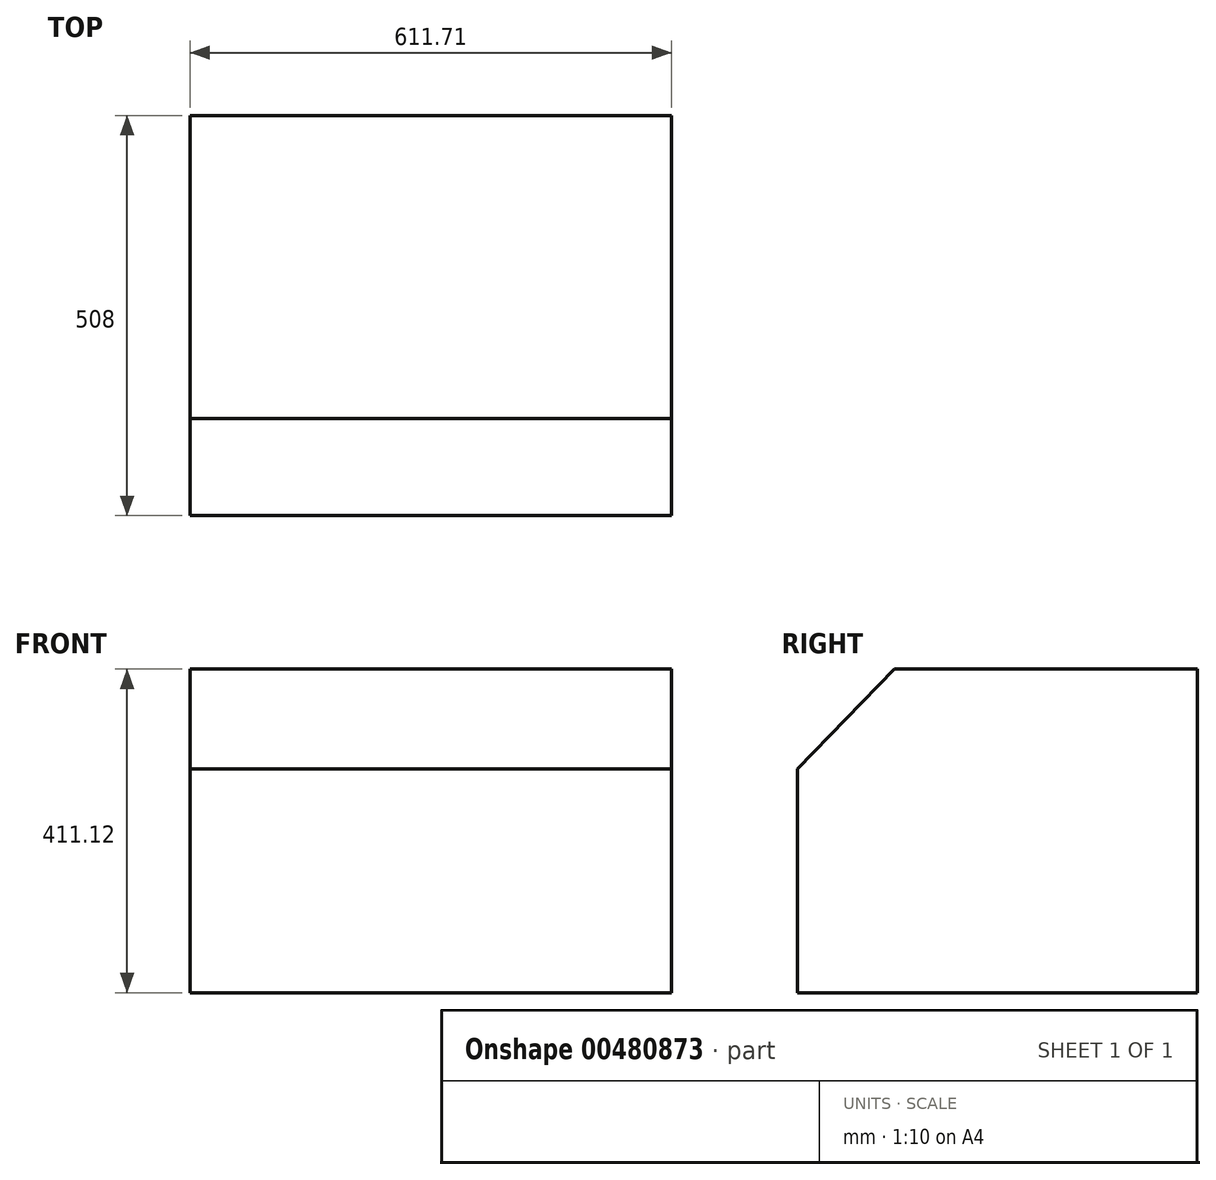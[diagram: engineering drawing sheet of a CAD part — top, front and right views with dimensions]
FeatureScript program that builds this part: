
annotation { "Feature Type Name" : "Feature", "Feature Type Description" : "" }
export const myFeature = defineFeature(function(context is Context, id is Id, definition is map)
    precondition{}
    {
        {
            var Q0;
            Q0=qCreatedBy(makeId("Front.planeOp"),FACE);
            var sketch = newSketch(context, id + "F0", { "sketchPlane" : qUnion([Q0])});
            skLineSegment(sketch, "E0.bottom", {"start": v(-269.54, 139.23) * mm, "end": v(342.17, 139.23) * mm});
            skLineSegment(sketch, "E0.top", {"start": v(-269.54, -144.89) * mm, "end": v(342.17, -144.89) * mm});
            skLineSegment(sketch, "E0.left", {"start": v(-269.54, 139.23) * mm, "end": v(-269.54, -144.89) * mm});
            skLineSegment(sketch, "E0.right", {"start": v(342.17, 139.23) * mm, "end": v(342.17, -144.89) * mm});
            skSolve(sketch);
        }
        {
            var Q0;
            Q0 = qSketchRegion(id + "F0", true);
            extrude(context, id + "F1", {"entities" : qUnion([Q0]), "depth" : 508 * mm});
        }
        {
            var Q0;
            Q0=makeQuery(id+"F1.opExtrude","SWEPT_FACE",FACE,{"disambiguationData":[OSD([sQuery(id+"F0.wireOp",EDGE,"E0.bottom")])]});
            var sketch = newSketch(context, id + "F2", { "sketchPlane" : qUnion([Q0])});
            skLineSegment(sketch, "E1.bottom", {"start": v(-269.54, -384.6) * mm, "end": v(342.17, -384.6) * mm});
            skLineSegment(sketch, "E1.top", {"start": v(-269.54, 0) * mm, "end": v(342.17, 0) * mm});
            skLineSegment(sketch, "E1.left", {"start": v(-269.54, -384.6) * mm, "end": v(-269.54, 0) * mm});
            skLineSegment(sketch, "E1.right", {"start": v(342.17, -384.6) * mm, "end": v(342.17, 0) * mm});
            skSolve(sketch);
        }
        {
            var Q0;
            Q0 = qSketchRegion(id + "F2", true);
            extrude(context, id + "F3", {"entities" : qUnion([Q0]), "operationType" : NewBodyOperationType.ADD, "depth" : 127 * mm});
        }
        {
            var Q0;
            Q0=makeQuery(id+"F3.boolean.opBoolean","MERGE",FACE,{"derivedFrom":[makeQuery(id+"F1.opExtrude","SWEPT_FACE",FACE,{"disambiguationData":[OSD([sQuery(id+"F0.wireOp",EDGE,"E0.right")])]}),makeQuery(id+"F3.opExtrude","SWEPT_FACE",FACE,{"disambiguationData":[OSD([sQuery(id+"F2.wireOp",EDGE,"E1.right")])]})]});
            var sketch = newSketch(context, id + "F4", { "sketchPlane" : qUnion([Q0])});
            skLineSegment(sketch, "E2", {"start": v(-384.6, 266.23) * mm, "end": v(-508, 139.23) * mm});
            skLineSegment(sketch, "E3", {"start": v(-508, 139.23) * mm, "end": v(-384.6, 139.23) * mm});
            skLineSegment(sketch, "E4", {"start": v(-384.6, 139.23) * mm, "end": v(-384.6, 266.23) * mm});
            skSolve(sketch);
        }
        {
            var Q0;
            Q0=makeQuery(id+"F3.boolean.opBoolean","MERGE",FACE,{"derivedFrom":[makeQuery(id+"F1.opExtrude","SWEPT_FACE",FACE,{"disambiguationData":[OSD([sQuery(id+"F0.wireOp",EDGE,"E0.left")])]}),makeQuery(id+"F3.opExtrude","SWEPT_FACE",FACE,{"disambiguationData":[OSD([sQuery(id+"F2.wireOp",EDGE,"E1.left")])]})]});
            var sketch = newSketch(context, id + "F5", { "sketchPlane" : qUnion([Q0])});
            skLineSegment(sketch, "E5", {"start": v(384.6, 266.23) * mm, "end": v(508, 139.23) * mm});
            skLineSegment(sketch, "E6", {"start": v(508, 139.23) * mm, "end": v(384.6, 139.23) * mm});
            skLineSegment(sketch, "E7", {"start": v(384.6, 139.23) * mm, "end": v(384.6, 266.23) * mm});
            skSolve(sketch);
        }
        {
            var Q0;
            Q0 = qSketchRegion(id + "F5", true);
            extrude(context, id + "F6", {"entities" : qUnion([Q0]), "operationType" : NewBodyOperationType.ADD, "oppositeDirection" : true, "depth" : 535.7 * mm});
        }
        {
            var Q0;
            Q0=makeQuery(id+"F4.imprint","IMPRINT",FACE,{"disambiguationData":[TD([[makeQuery(id+"F4.imprint","IMPRINT",EDGE,{"derivedFrom":sQuery(id+"F4.wireOp",EDGE,"E2")}),1.0]])]});
            extrude(context, id + "F7", {"entities" : qUnion([Q0]), "operationType" : NewBodyOperationType.ADD, "oppositeDirection" : true, "depth" : 254 * mm});
        }
    });
